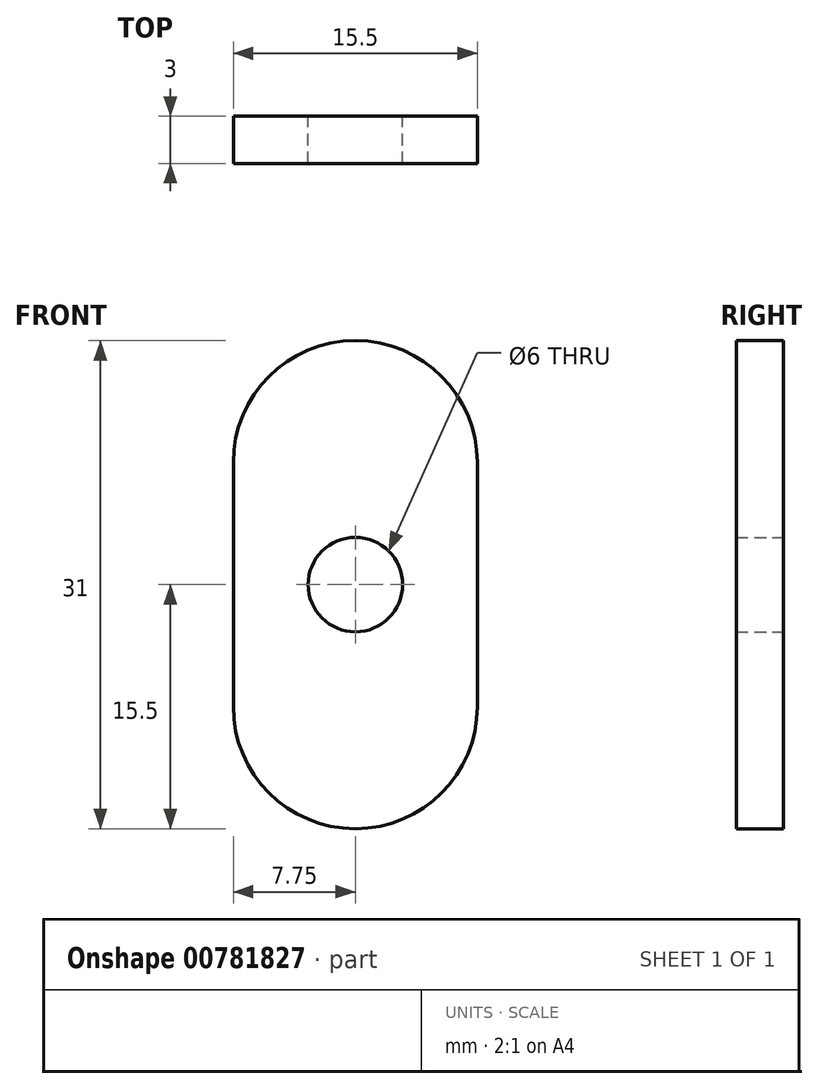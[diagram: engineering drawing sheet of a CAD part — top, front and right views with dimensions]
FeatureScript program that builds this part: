
annotation { "Feature Type Name" : "Feature", "Feature Type Description" : "" }
export const myFeature = defineFeature(function(context is Context, id is Id, definition is map)
    precondition{}
    {
        {
            var Q0;
            Q0=qCreatedBy(makeId("Front.planeOp"),FACE);
            var sketch = newSketch(context, id + "F0", { "sketchPlane" : qUnion([Q0])});
            skLineSegment(sketch, "E0.bottom", {"start": v(-7.75, 7.75) * mm, "end": v(7.75, 7.75) * mm});
            skLineSegment(sketch, "E0.top", {"start": v(-7.75, -7.75) * mm, "end": v(7.75, -7.75) * mm});
            skLineSegment(sketch, "E0.left", {"start": v(-7.75, 7.75) * mm, "end": v(-7.75, -7.75) * mm});
            skLineSegment(sketch, "E0.right", {"start": v(7.75, 7.75) * mm, "end": v(7.75, -7.75) * mm});
            skPoint(sketch, "E0.middle", {"position": v(0, 0) * mm});
            skArc(sketch, "E1", {"start": v(-7.75, 7.75) * mm, "mid": v(0, 15.5) * mm, "end": v(7.75, 7.75) * mm});
            skArc(sketch, "E2", {"start": v(7.75, -7.75) * mm, "mid": v(0, -15.5) * mm, "end": v(-7.75, -7.75) * mm});
            skCircle(sketch, "E3", {"center": v(0, 0) * mm, "radius": 3 * mm});
            skSolve(sketch);
        }
        {
            var Q0;
            Q0 = qSketchRegion(id + "F0", true);
            extrude(context, id + "F1", {"entities" : qUnion([Q0]), "depth" : 3 * mm, "offsetDistance" : 25 * mm});
        }
    });
